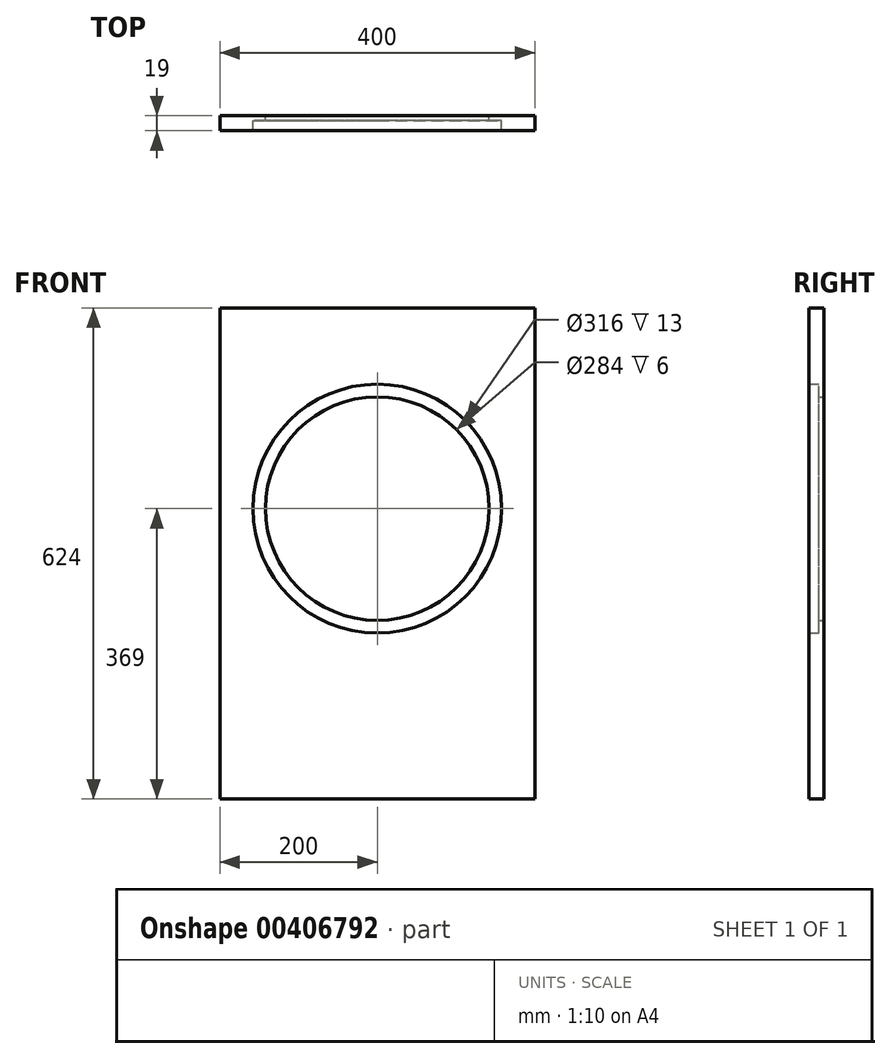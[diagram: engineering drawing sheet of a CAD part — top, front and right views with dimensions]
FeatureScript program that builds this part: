
annotation { "Feature Type Name" : "Feature", "Feature Type Description" : "" }
export const myFeature = defineFeature(function(context is Context, id is Id, definition is map)
    precondition{}
    {
        {
            var Q0;
            Q0=qCreatedBy(makeId("Front.planeOp"),FACE);
            var sketch = newSketch(context, id + "F0", { "sketchPlane" : qUnion([Q0])});
            skLineSegment(sketch, "E0.bottom", {"start": v(0, 0) * mm, "end": v(400, 0) * mm});
            skLineSegment(sketch, "E0.top", {"start": v(0, 624) * mm, "end": v(400, 624) * mm});
            skLineSegment(sketch, "E0.left", {"start": v(0, 0) * mm, "end": v(0, 624) * mm});
            skLineSegment(sketch, "E0.right", {"start": v(400, 0) * mm, "end": v(400, 624) * mm});
            skCircle(sketch, "E1", {"center": v(200, 369) * mm, "radius": 142 * mm});
            skCircle(sketch, "E2", {"center": v(200, 369) * mm, "radius": 158 * mm});
            skSolve(sketch);
        }
        {
            var Q0;
            Q0=makeQuery(id+"F0.imprint","IMPRINT",FACE,{"disambiguationData":[TD([[makeQuery(id+"F0.imprint","IMPRINT",EDGE,{"derivedFrom":sQuery(id+"F0.wireOp",EDGE,"E0.bottom")}),1.0]])]});
            extrude(context, id + "F1", {"entities" : qUnion([Q0]), "depth" : 19 * mm, "offsetDistance" : 25 * mm});
        }
        {
            var Q0;
            Q0=makeQuery(id+"F0.imprint","IMPRINT",FACE,{"disambiguationData":[TD([[makeQuery(id+"F0.imprint","IMPRINT",EDGE,{"derivedFrom":sQuery(id+"F0.wireOp",EDGE,"E1")}),-1.0]])]});
            extrude(context, id + "F2", {"entities" : qUnion([Q0]), "operationType" : NewBodyOperationType.ADD, "depth" : 6 * mm, "offsetDistance" : 25 * mm});
        }
    });
